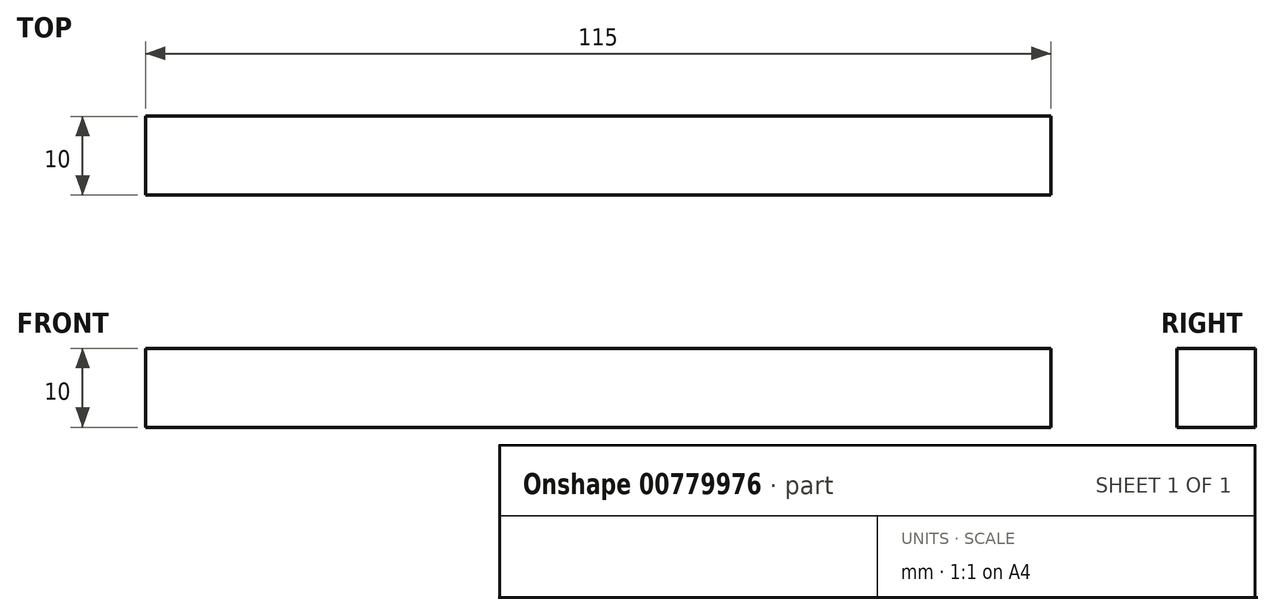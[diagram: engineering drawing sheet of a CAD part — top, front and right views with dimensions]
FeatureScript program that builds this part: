
annotation { "Feature Type Name" : "Feature", "Feature Type Description" : "" }
export const myFeature = defineFeature(function(context is Context, id is Id, definition is map)
    precondition{}
    {
        {
            var Q0;
            Q0=qCreatedBy(makeId("Top.planeOp"),FACE);
            var sketch = newSketch(context, id + "F0", { "sketchPlane" : qUnion([Q0])});
            skLineSegment(sketch, "E0", {"start": v(-52.8, 20.62) * mm, "end": v(62.2, 20.62) * mm});
            skLineSegment(sketch, "E1", {"start": v(62.2, 20.62) * mm, "end": v(62.2, 10.62) * mm});
            skLineSegment(sketch, "E2", {"start": v(62.2, 10.62) * mm, "end": v(-52.8, 10.62) * mm});
            skLineSegment(sketch, "E3", {"start": v(-52.8, 10.62) * mm, "end": v(-52.8, 20.62) * mm});
            skSolve(sketch);
        }
        {
            var Q0;
            Q0=qSketchRegion(id+"F0",true);
            extrude(context, id + "F1", {"entities" : qUnion([Q0]), "depth" : 10 * mm, "offsetDistance" : 25 * mm});
        }
    });
